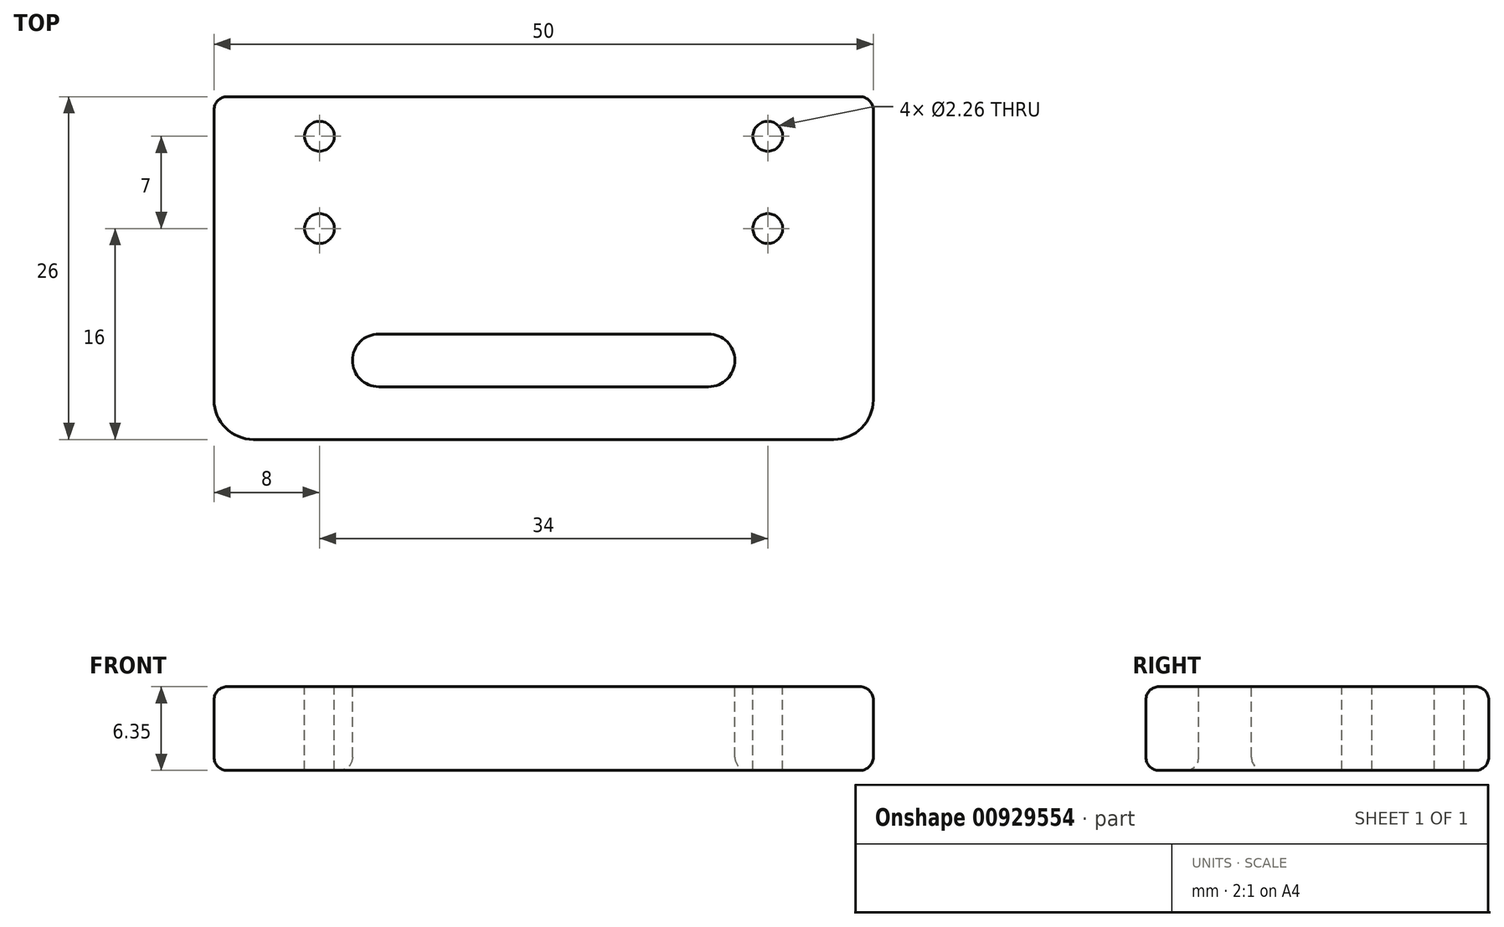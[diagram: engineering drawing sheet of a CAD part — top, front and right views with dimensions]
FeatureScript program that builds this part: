
annotation { "Feature Type Name" : "Feature", "Feature Type Description" : "" }
export const myFeature = defineFeature(function(context is Context, id is Id, definition is map)
    precondition{}
    {
        {
            var Q0;
            Q0=qCreatedBy(makeId("Top.planeOp"),FACE);
            var sketch = newSketch(context, id + "F0", { "sketchPlane" : qUnion([Q0])});
            skLineSegment(sketch, "E0.bottom", {"start": v(-25, 13) * mm, "end": v(25, 13) * mm});
            skLineSegment(sketch, "E0.top", {"start": v(-25, -13) * mm, "end": v(25, -13) * mm});
            skLineSegment(sketch, "E0.left", {"start": v(-25, 13) * mm, "end": v(-25, -13) * mm});
            skLineSegment(sketch, "E0.right", {"start": v(25, 13) * mm, "end": v(25, -13) * mm});
            skPoint(sketch, "E0.middle", {"position": v(0, 0) * mm});
            skSolve(sketch);
        }
        {
            var Q0;
            Q0 = qSketchRegion(id + "F0", true);
            extrude(context, id + "F1", {"entities" : qUnion([Q0]), "depth" : 6.35 * mm, "offsetDistance" : 25.4 * mm});
        }
        {
            var Q0;
            Q0=makeQuery(id+"F1.opExtrude","CAP_FACE",FACE,{"disambiguationData":[OSD([sQuery(id+"F0.wireOp",EDGE,"E0.bottom"),sQuery(id+"F0.wireOp",EDGE,"E0.top"),sQuery(id+"F0.wireOp",EDGE,"E0.left"),sQuery(id+"F0.wireOp",EDGE,"E0.right")])],"isStart":false});
            var sketch = newSketch(context, id + "F2", { "sketchPlane" : qUnion([Q0])});
            skLineSegment(sketch, "E1.bottom", {"start": v(-17, 10) * mm, "end": v(17, 10) * mm, "construction": true});
            skLineSegment(sketch, "E1.top", {"start": v(-17, 3) * mm, "end": v(17, 3) * mm, "construction": true});
            skLineSegment(sketch, "E1.left", {"start": v(-17, 10) * mm, "end": v(-17, 3) * mm, "construction": true});
            skLineSegment(sketch, "E1.right", {"start": v(17, 10) * mm, "end": v(17, 3) * mm, "construction": true});
            skLineSegment(sketch, "E2", {"start": v(0, 0) * mm, "end": v(0, 10) * mm, "construction": true});
            skCircle(sketch, "E3", {"center": v(-17, 10) * mm, "radius": 1.13 * mm});
            skCircle(sketch, "E4", {"center": v(-17, 3) * mm, "radius": 1.13 * mm});
            skCircle(sketch, "E5", {"center": v(17, 3) * mm, "radius": 1.13 * mm});
            skCircle(sketch, "E6", {"center": v(17, 10) * mm, "radius": 1.13 * mm});
            skSolve(sketch);
        }
        {
            var Q0;
            Q0 = qSketchRegion(id + "F2", true);
            extrude(context, id + "F3", {"entities" : qUnion([Q0]), "operationType" : NewBodyOperationType.REMOVE, "endBound" : BoundingType.THROUGH_ALL, "oppositeDirection" : true, "depth" : 25.4 * mm, "offsetDistance" : 25.4 * mm});
        }
        {
            var Q0;
            Q0=makeQuery(id+"F1.opExtrude","CAP_FACE",FACE,{"disambiguationData":[OSD([sQuery(id+"F0.wireOp",EDGE,"E0.bottom"),sQuery(id+"F0.wireOp",EDGE,"E0.top"),sQuery(id+"F0.wireOp",EDGE,"E0.left"),sQuery(id+"F0.wireOp",EDGE,"E0.right")])],"isStart":false});
            var sketch = newSketch(context, id + "F4", { "sketchPlane" : qUnion([Q0])});
            skLineSegment(sketch, "E7", {"start": v(-12.5, -7) * mm, "end": v(12.5, -7) * mm, "construction": true});
            skLineSegment(sketch, "E8", {"start": v(0, -7) * mm, "end": v(0, 0) * mm, "construction": true});
            skArc(sketch, "E9", {"start": v(-12.5, -5) * mm, "mid": v(-14.5, -7) * mm, "end": v(-12.5, -9) * mm});
            skArc(sketch, "E10", {"start": v(12.5, -5) * mm, "mid": v(14.5, -7) * mm, "end": v(12.5, -9) * mm});
            skLineSegment(sketch, "E11", {"start": v(-12.5, -5) * mm, "end": v(12.5, -5) * mm});
            skLineSegment(sketch, "E12", {"start": v(12.5, -9) * mm, "end": v(-12.5, -9) * mm});
            skSolve(sketch);
        }
        {
            var Q0;
            Q0 = qSketchRegion(id + "F4", true);
            extrude(context, id + "F5", {"entities" : qUnion([Q0]), "operationType" : NewBodyOperationType.REMOVE, "endBound" : BoundingType.THROUGH_ALL, "oppositeDirection" : true, "depth" : 25.4 * mm, "offsetDistance" : 25.4 * mm});
        }
        {
            var Q0;
            Q0=makeQuery(id+"F1.opExtrude","SWEPT_EDGE",EDGE,{"disambiguationData":[OSD([sQuery(id+"F0.wireOp",EDGE,"E0.bottom"),sQuery(id+"F0.wireOp",EDGE,"E0.left")])]});
            var Q1;
            Q1=makeQuery(id+"F1.opExtrude","SWEPT_EDGE",EDGE,{"disambiguationData":[OSD([sQuery(id+"F0.wireOp",EDGE,"E0.bottom"),sQuery(id+"F0.wireOp",EDGE,"E0.right")])]});
            var Q2;
            Q2=makeQuery(id+"F5.boolean.opBoolean","COPY",EDGE,{"derivedFrom":makeQuery(id+"F5.opExtrude","CAP_EDGE",EDGE,{"disambiguationData":[OSD([sQuery(id+"F4.wireOp",EDGE,"E11")])],"isStart":true})});
            var Q3;
            Q3=makeQuery(id+"F5.boolean.opBoolean","INTERSECT",EDGE,{"derivedFrom":[makeQuery(id+"F1.opExtrude","CAP_FACE",FACE,{"disambiguationData":[OSD([sQuery(id+"F0.wireOp",EDGE,"E0.bottom"),sQuery(id+"F0.wireOp",EDGE,"E0.top"),sQuery(id+"F0.wireOp",EDGE,"E0.left"),sQuery(id+"F0.wireOp",EDGE,"E0.right")])],"isStart":true}),makeQuery(id+"F5.opExtrude","SWEPT_FACE",FACE,{"disambiguationData":[OSD([sQuery(id+"F4.wireOp",EDGE,"E11")])]})]});
            fillet(context, id + "F6", {"entities" : qUnion([Q0, Q1, Q2, Q3]), "radius" : 1 * mm, "tangentPropagation" : true, "allowEdgeOverflow" : false});
        }
        {
            var Q0;
            Q0=makeQuery(id+"F1.opExtrude","SWEPT_EDGE",EDGE,{"disambiguationData":[OSD([sQuery(id+"F0.wireOp",EDGE,"E0.top"),sQuery(id+"F0.wireOp",EDGE,"E0.left")])]});
            var Q1;
            Q1=makeQuery(id+"F1.opExtrude","SWEPT_EDGE",EDGE,{"disambiguationData":[OSD([sQuery(id+"F0.wireOp",EDGE,"E0.top"),sQuery(id+"F0.wireOp",EDGE,"E0.right")])]});
            fillet(context, id + "F7", {"entities" : qUnion([Q0, Q1]), "radius" : 3 * mm, "tangentPropagation" : true, "allowEdgeOverflow" : false});
        }
        {
            var Q0;
            Q0=makeQuery(id+"F1.opExtrude","CAP_EDGE",EDGE,{"disambiguationData":[OSD([sQuery(id+"F0.wireOp",EDGE,"E0.left")])],"isStart":false});
            var Q1;
            Q1=makeQuery(id+"F1.opExtrude","CAP_EDGE",EDGE,{"disambiguationData":[OSD([sQuery(id+"F0.wireOp",EDGE,"E0.left")])],"isStart":true});
            fillet(context, id + "F8", {"entities" : qUnion([Q0, Q1]), "radius" : 1 * mm, "tangentPropagation" : true, "allowEdgeOverflow" : false});
        }
    });
